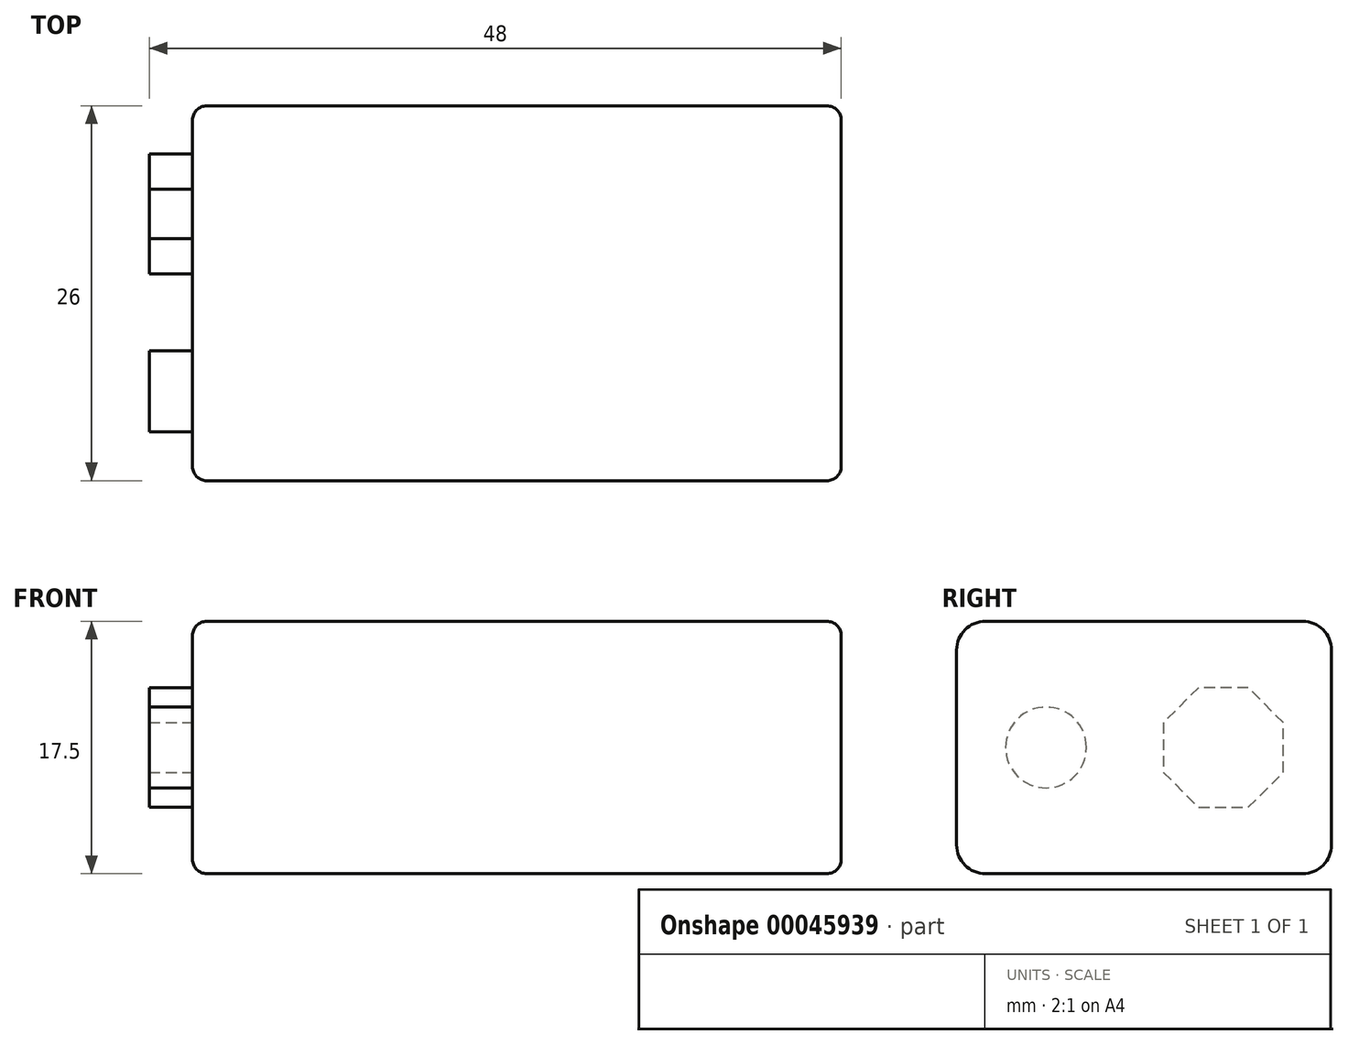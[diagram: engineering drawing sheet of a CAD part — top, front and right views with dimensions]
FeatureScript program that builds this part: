
annotation { "Feature Type Name" : "Feature", "Feature Type Description" : "" }
export const myFeature = defineFeature(function(context is Context, id is Id, definition is map)
    precondition{}
    {
        {
            var Q0;
            Q0=qCreatedBy(makeId("Top.planeOp"),FACE);
            var sketch = newSketch(context, id + "F0", { "sketchPlane" : qUnion([Q0])});
            skLineSegment(sketch, "E0.rect.bottom", {"start": v(22.5, 13) * mm, "end": v(-22.5, 13) * mm});
            skLineSegment(sketch, "E0.rect.top", {"start": v(22.5, -13) * mm, "end": v(-22.5, -13) * mm});
            skLineSegment(sketch, "E0.rect.left", {"start": v(22.5, 13) * mm, "end": v(22.5, -13) * mm});
            skLineSegment(sketch, "E0.rect.right", {"start": v(-22.5, 13) * mm, "end": v(-22.5, -13) * mm});
            skPoint(sketch, "E0.rect.middle", {"position": v(0, 0) * mm});
            skSolve(sketch);
        }
        {
            var Q0;
            Q0=qSketchRegion(id+"F0",true);
            extrude(context, id + "F1", {"entities" : qUnion([Q0]), "depth" : 17.5 * mm});
        }
        {
            var Q0;
            Q0=makeQuery(id+"F1.opExtrude","SWEPT_FACE",FACE,{"disambiguationData":[OSD([sQuery(id+"F0.wireOp",EDGE,"E0.rect.right")])]});
            var sketch = newSketch(context, id + "F2", { "sketchPlane" : qUnion([Q0])});
            skCircle(sketch, "E1", {"center": v(6.8, 8.75) * mm, "radius": 2.8 * mm});
            skLineSegment(sketch, "E2", {"start": v(-13, 8.75) * mm, "end": v(13, 8.75) * mm, "construction": true});
            skCircle(sketch, "E3.cCircle", {"center": v(-5.5, 8.75) * mm, "radius": 4.5 * mm, "construction": true});
            skLineSegment(sketch, "E3.0", {"start": v(-3.78, 4.6) * mm, "end": v(-7.22, 4.6) * mm});
            skLineSegment(sketch, "E3.1", {"start": v(-7.22, 4.6) * mm, "end": v(-9.66, 7.03) * mm});
            skLineSegment(sketch, "E3.2", {"start": v(-9.66, 7.03) * mm, "end": v(-9.66, 10.47) * mm});
            skLineSegment(sketch, "E3.3", {"start": v(-9.66, 10.47) * mm, "end": v(-7.22, 12.9) * mm});
            skLineSegment(sketch, "E3.4", {"start": v(-7.22, 12.9) * mm, "end": v(-3.78, 12.9) * mm});
            skLineSegment(sketch, "E3.5", {"start": v(-3.78, 12.9) * mm, "end": v(-1.34, 10.47) * mm});
            skLineSegment(sketch, "E3.6", {"start": v(-1.34, 10.47) * mm, "end": v(-1.34, 7.03) * mm});
            skLineSegment(sketch, "E3.7", {"start": v(-1.34, 7.03) * mm, "end": v(-3.78, 4.6) * mm});
            skSolve(sketch);
        }
        {
            var Q0;
            Q0=qSketchRegion(id+"F2",true);
            extrude(context, id + "F3", {"entities" : qUnion([Q0]), "operationType" : NewBodyOperationType.ADD, "depth" : 3 * mm});
        }
        {
            var Q0;
            Q0=makeQuery(id+"F1.opExtrude","CAP_EDGE",EDGE,{"disambiguationData":[OSD([sQuery(id+"F0.wireOp",EDGE,"E0.rect.bottom")])],"isStart":false});
            var Q1;
            Q1=makeQuery(id+"F1.opExtrude","CAP_EDGE",EDGE,{"disambiguationData":[OSD([sQuery(id+"F0.wireOp",EDGE,"E0.rect.bottom")])],"isStart":true});
            var Q2;
            Q2=makeQuery(id+"F1.opExtrude","CAP_EDGE",EDGE,{"disambiguationData":[OSD([sQuery(id+"F0.wireOp",EDGE,"E0.rect.top")])],"isStart":false});
            var Q3;
            Q3=makeQuery(id+"F1.opExtrude","CAP_EDGE",EDGE,{"disambiguationData":[OSD([sQuery(id+"F0.wireOp",EDGE,"E0.rect.top")])],"isStart":true});
            fillet(context, id + "F4", {"entities" : qUnion([Q0, Q1, Q2, Q3]), "radius" : 2 * mm, "tangentPropagation" : true, "allowEdgeOverflow" : false});
        }
        {
            var Q0;
            Q0=makeQuery(id+"F1.opExtrude","CAP_EDGE",EDGE,{"disambiguationData":[OSD([sQuery(id+"F0.wireOp",EDGE,"E0.rect.right")])],"isStart":false});
            var Q1;
            Q1=makeQuery(id+"F1.opExtrude","CAP_EDGE",EDGE,{"disambiguationData":[OSD([sQuery(id+"F0.wireOp",EDGE,"E0.rect.left")])],"isStart":false});
            fillet(context, id + "F5", {"entities" : qUnion([Q0, Q1]), "radius" : 1 * mm, "tangentPropagation" : true, "allowEdgeOverflow" : false});
        }
    });
